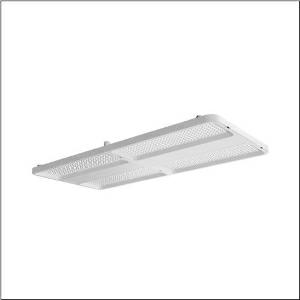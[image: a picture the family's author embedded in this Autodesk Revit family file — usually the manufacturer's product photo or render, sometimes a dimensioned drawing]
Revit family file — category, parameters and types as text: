
# Revit family: highbay_11_maxi_51hn11db4lda
name_source: partatom
category: Lighting Fixtures
units: mm (PartAtom-declared; Revit-internal decimal feet)

## family parameters
Cut with Voids When Loaded = No
Host = Face
Light Source = No
Part Type = Normal
Room Calculation Point = No
Round Connector Dimension = Use Diameter
Shared = No

## types (1)
- --- (1 x LED, 3960 lm, 19.5 W, 4000K)
    Apparent Load = 20 VA
    CIE Flux Codes = 85 97 100 100 100
    Color Rendering = 80
    Color Temperature = 4000K
    Default Elevation = 1800 mm
    Description = high bay luminaire Highbay 11 maxi; direct symmetric narrow distribution, light control with lens of PMMA; UGR ≤ 19 (X = 4H | Y = 8H | S = 0.25H | reflection values 70/50/20); luminous flux: 26.000lm; light colour: 840, colour temperature: 4000K, MacAdam ≤ 2 SDCM (initial), colour rendering: CRI > 80; luminous efficacy: 207,3lm/W; rated service life: 100.000h (L95) at AT= 25°C; control: DALI 2; luminaire connection: terminal, 5-pole, max. 2.5mm² (cable entry for one cable, Ø 8.5..16mm); mains connection: 230..240V, AC/DC 0/50..60Hz; connected load: 125,4W; protection rating (complete): IP66; insulation class (complete): insulation class I (protective earthing); protection symbol: D; impact resistance: IK08; certification: CE, ENEC, VDE, UKCA; luminaire for central battery installations according to EN 60598-2-22, internal wiring halogen-free; luminaire Suitable for use in the food industry according to the specifications of IFS-Food, HACCP and/or BRC; LABS conformity tested according to VDMA 24364:2018-05; housing frame of high-performance plastic PA6, matt traffic white (RAL 9016); cover of PMMA; dimension (LxWxH): 946 x 442 x 72mm; permissible operating ambient temperature: -40..+65°C (reducing of maximum allowable ambient temperature of 5°C with ceiling mounting); packaging unit: 1 piece; (delivery without accessories; please order mounting accessories separately)
    Height = 72 mm  [stored 0.23622 ft]
    Lamp = 1 x LED
    Lamp Light Flux = 3960 lm
    Lamp Power = 19.5 W
    Lamp count = 1
    Length = 946 mm
    Luminous efficacy = 203 lm/W
    Manufacturer = Siteco
    ModVariant = No
    Model = 51HN11DB4LDA
    Mounting Place = Ceiling
    Mounting Type = Pendant
    Number of Poles = 1
    OnlyDefault = Yes
    Power Factor = 1
    Product Name = Highbay 11 maxi
    Product group = high bay luminaire
    ProductGroupID = 902
    Protection Class = Protection class I
    Protection Degree = IP 66
    RLX_Detail_Level = 1
    RLX_Emergency_Light_Flux = 0 lm
    RLX_Emergency_Type = 0
    RLX_Emergency_Type_DB = No
    RlxData = <blob elided: 127089 chars, md5=d446d7c6>
    Socket = socket
    Standby Power = 0 W
    System Light Flux = 3960 lm
    System Power = 20 W
    Type Comments = : DC mode (central or group accumulator) initial emergency light level
    Type Image = l_1363244.jpg
    URL = http://relux.com
    VarID = @adj_022145
    Voltage = 0 V
    Weight = 0.00 kg
    Width = 442 mm

note: [stored X ft] marks values corroborated as IEEE doubles in the binary element streams (Revit-internal decimal feet)

## geometry (parser evidence)
native form markers: Blend x4, Sweep x12
no freeform markers — native parametric forms only
